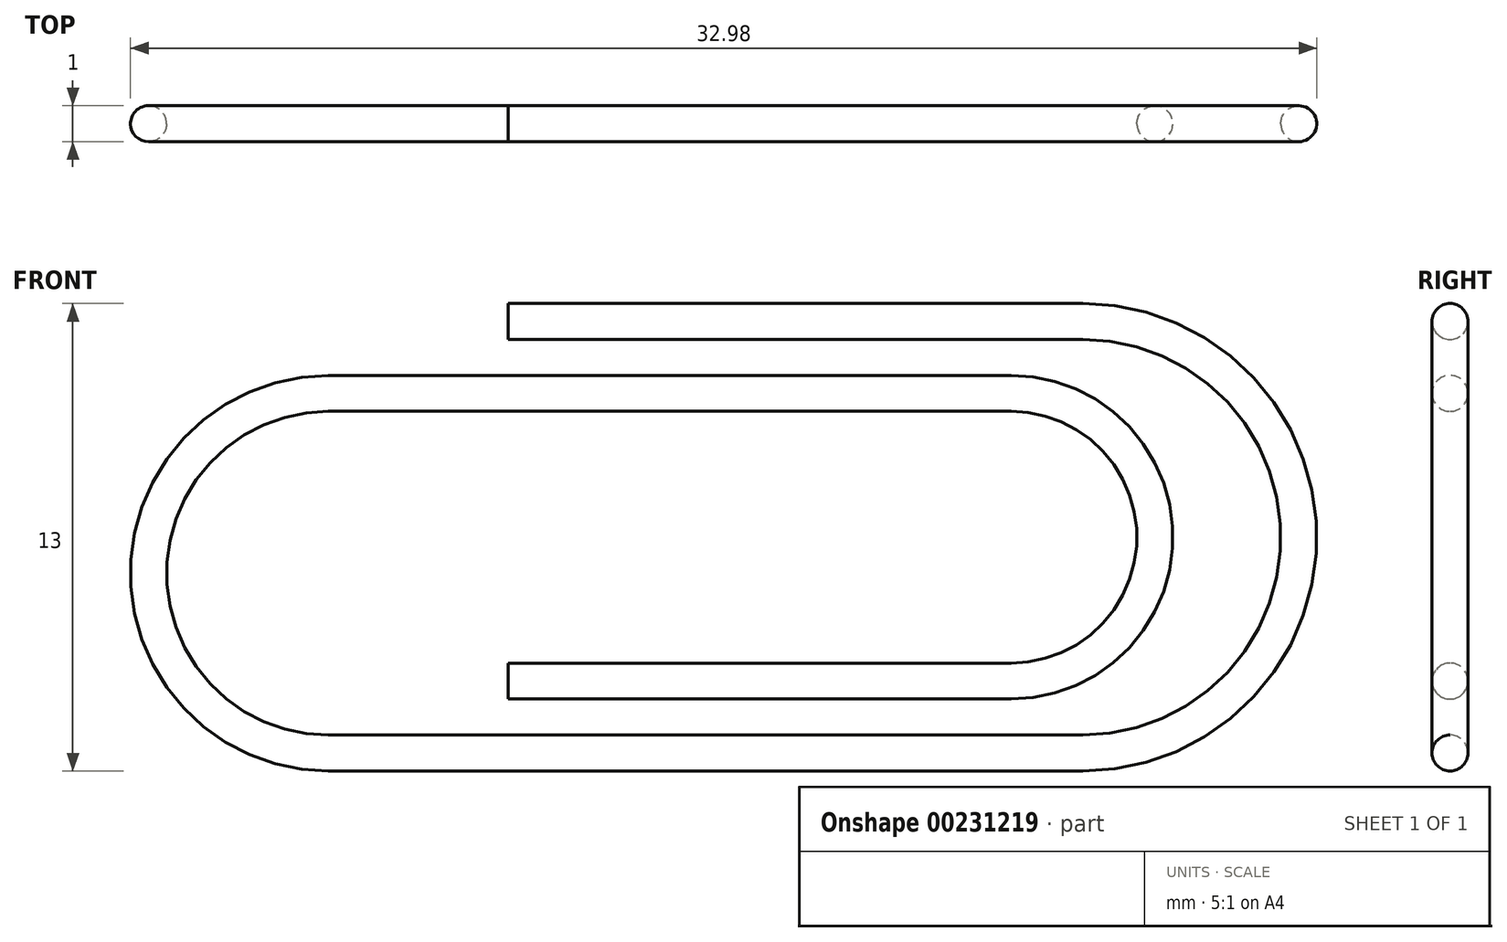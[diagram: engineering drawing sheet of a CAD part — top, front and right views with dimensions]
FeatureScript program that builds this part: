
annotation { "Feature Type Name" : "Feature", "Feature Type Description" : "" }
export const myFeature = defineFeature(function(context is Context, id is Id, definition is map)
    precondition{}
    {
        {
            var Q0;
            Q0=qCreatedBy(makeId("Front.planeOp"),FACE);
            var sketch = newSketch(context, id + "F0", { "sketchPlane" : qUnion([Q0])});
            skLineSegment(sketch, "E0", {"start": v(0, 0) * mm, "end": v(15.98, 0) * mm});
            skArc(sketch, "E1", {"start": v(15.98, 0) * mm, "mid": v(21.98, -6) * mm, "end": v(15.98, -12) * mm});
            skLineSegment(sketch, "E2", {"start": v(15.98, -12) * mm, "end": v(-5, -12) * mm});
            skArc(sketch, "E3", {"start": v(-5, -12) * mm, "mid": v(-10, -7) * mm, "end": v(-5, -2) * mm});
            skLineSegment(sketch, "E4", {"start": v(-5, -2) * mm, "end": v(13.98, -2) * mm});
            skArc(sketch, "E5", {"start": v(13.98, -2) * mm, "mid": v(17.98, -6) * mm, "end": v(13.98, -10) * mm});
            skLineSegment(sketch, "E6", {"start": v(13.98, -10) * mm, "end": v(0, -10) * mm});
            skLineSegment(sketch, "E7", {"start": v(0, 0) * mm, "end": v(0, -15.15) * mm, "construction": true});
            skSolve(sketch);
        }
        {
            var Q0;
            Q0=qCreatedBy(makeId("Right.planeOp"),FACE);
            var sketch = newSketch(context, id + "F1", { "sketchPlane" : qUnion([Q0])});
            skCircle(sketch, "E8", {"center": v(0, 0) * mm, "radius": 0.5 * mm});
            skSolve(sketch);
        }
        {
            var Q0;
            Q0 = qSketchRegion(id + "F1", true);
            var Q1;
            Q1=sQuery(id+"F0.wireOp",EDGE,"E0");
            var Q2;
            Q2=sQuery(id+"F0.wireOp",EDGE,"E1");
            var Q3;
            Q3=sQuery(id+"F0.wireOp",EDGE,"E2");
            var Q4;
            Q4=sQuery(id+"F0.wireOp",EDGE,"E3");
            var Q5;
            Q5=sQuery(id+"F0.wireOp",EDGE,"E4");
            var Q6;
            Q6=sQuery(id+"F0.wireOp",EDGE,"E5");
            var Q7;
            Q7=sQuery(id+"F0.wireOp",EDGE,"E6");
            sweep(context, id + "F2", {"profiles" : qUnion([Q0]), "path" : qUnion([Q1, Q2, Q3, Q4, Q5, Q6, Q7])});
        }
    });
